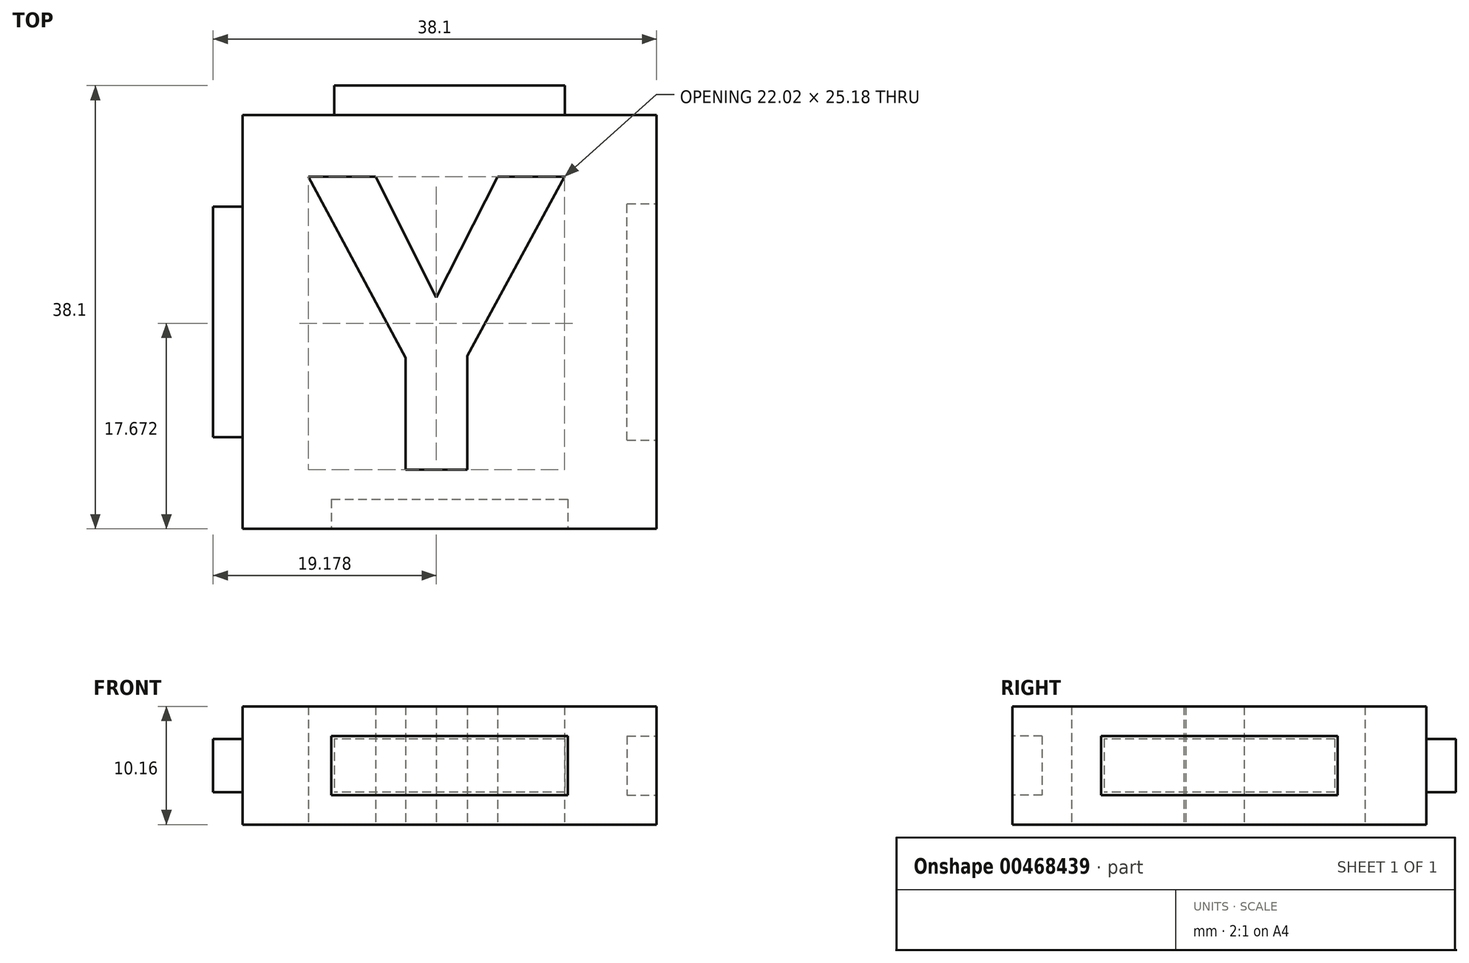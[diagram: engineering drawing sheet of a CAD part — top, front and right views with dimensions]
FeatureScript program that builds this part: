
annotation { "Feature Type Name" : "Feature", "Feature Type Description" : "" }
export const myFeature = defineFeature(function(context is Context, id is Id, definition is map)
    precondition{}
    {
        {
            var Q0;
            Q0=qCreatedBy(makeId("Top.planeOp"),FACE);
            var sketch = newSketch(context, id + "F0", { "sketchPlane" : qUnion([Q0])});
            skLineSegment(sketch, "E0.bottom", {"start": v(-17.78, 17.78) * mm, "end": v(17.78, 17.78) * mm});
            skLineSegment(sketch, "E0.top", {"start": v(-17.78, -17.78) * mm, "end": v(17.78, -17.78) * mm});
            skLineSegment(sketch, "E0.left", {"start": v(-17.78, 17.78) * mm, "end": v(-17.78, -17.78) * mm});
            skLineSegment(sketch, "E0.right", {"start": v(17.78, 17.78) * mm, "end": v(17.78, -17.78) * mm});
            skText(sketch, "E1", { "text": "Y", "fontName": "OpenSans-Bold.ttf"});
            const initialGuessF0  = {"E1": [-0.01215, -0.0127, 1, 0, 0.0254]};
            skSetInitialGuess(sketch, initialGuessF0);
            skSolve(sketch);
        }
        {
            var Q0;
            Q0=qSketchRegion(id+"F0",true);
            extrude(context, id + "F1", {"entities" : qUnion([Q0]), "endBound" : BoundingType.SYMMETRIC, "depth" : 10.16 * mm});
        }
        {
            var Q0;
            Q0=makeQuery(id+"F1.opExtrude","SWEPT_FACE",FACE,{"disambiguationData":[OSD([sQuery(id+"F0.wireOp",EDGE,"E0.bottom")])]});
            var sketch = newSketch(context, id + "F2", { "sketchPlane" : qUnion([Q0])});
            skLineSegment(sketch, "E2.bottom", {"start": v(-9.9, 2.29) * mm, "end": v(9.9, 2.29) * mm});
            skLineSegment(sketch, "E2.top", {"start": v(-9.9, -2.29) * mm, "end": v(9.9, -2.29) * mm});
            skLineSegment(sketch, "E2.left", {"start": v(-9.9, 2.29) * mm, "end": v(-9.9, -2.29) * mm});
            skLineSegment(sketch, "E2.right", {"start": v(9.9, 2.29) * mm, "end": v(9.9, -2.29) * mm});
            skSolve(sketch);
        }
        {
            var Q0;
            Q0=qSketchRegion(id+"F2",true);
            extrude(context, id + "F3", {"entities" : qUnion([Q0]), "operationType" : NewBodyOperationType.ADD, "depth" : 2.54 * mm});
        }
        {
            var Q0;
            Q0=makeQuery(id+"F1.opExtrude","SWEPT_FACE",FACE,{"disambiguationData":[OSD([sQuery(id+"F0.wireOp",EDGE,"E0.left")])]});
            var sketch = newSketch(context, id + "F4", { "sketchPlane" : qUnion([Q0])});
            skLineSegment(sketch, "E3.bottom", {"start": v(-9.9, 2.29) * mm, "end": v(9.9, 2.29) * mm});
            skLineSegment(sketch, "E3.top", {"start": v(-9.9, -2.29) * mm, "end": v(9.9, -2.29) * mm});
            skLineSegment(sketch, "E3.left", {"start": v(-9.9, 2.29) * mm, "end": v(-9.9, -2.29) * mm});
            skLineSegment(sketch, "E3.right", {"start": v(9.9, 2.29) * mm, "end": v(9.9, -2.29) * mm});
            skSolve(sketch);
        }
        {
            var Q0;
            Q0=qSketchRegion(id+"F4",true);
            extrude(context, id + "F5", {"entities" : qUnion([Q0]), "operationType" : NewBodyOperationType.ADD, "depth" : 2.54 * mm});
        }
        {
            var Q0;
            Q0=makeQuery(id+"F1.opExtrude","SWEPT_FACE",FACE,{"disambiguationData":[OSD([sQuery(id+"F0.wireOp",EDGE,"E0.top")])]});
            var sketch = newSketch(context, id + "F6", { "sketchPlane" : qUnion([Q0])});
            skLineSegment(sketch, "E4.bottom", {"start": v(-10.16, 2.54) * mm, "end": v(10.16, 2.54) * mm});
            skLineSegment(sketch, "E4.top", {"start": v(-10.16, -2.54) * mm, "end": v(10.16, -2.54) * mm});
            skLineSegment(sketch, "E4.left", {"start": v(-10.16, 2.54) * mm, "end": v(-10.16, -2.54) * mm});
            skLineSegment(sketch, "E4.right", {"start": v(10.16, 2.54) * mm, "end": v(10.16, -2.54) * mm});
            skSolve(sketch);
        }
        {
            var Q0;
            Q0=qSketchRegion(id+"F6",true);
            extrude(context, id + "F7", {"entities" : qUnion([Q0]), "operationType" : NewBodyOperationType.REMOVE, "oppositeDirection" : true, "depth" : 2.54 * mm});
        }
        {
            var Q0;
            Q0=makeQuery(id+"F1.opExtrude","SWEPT_FACE",FACE,{"disambiguationData":[OSD([sQuery(id+"F0.wireOp",EDGE,"E0.right")])]});
            var sketch = newSketch(context, id + "F8", { "sketchPlane" : qUnion([Q0])});
            skLineSegment(sketch, "E5.bottom", {"start": v(-10.16, 2.54) * mm, "end": v(10.16, 2.54) * mm});
            skLineSegment(sketch, "E5.top", {"start": v(-10.16, -2.54) * mm, "end": v(10.16, -2.54) * mm});
            skLineSegment(sketch, "E5.left", {"start": v(-10.16, 2.54) * mm, "end": v(-10.16, -2.54) * mm});
            skLineSegment(sketch, "E5.right", {"start": v(10.16, 2.54) * mm, "end": v(10.16, -2.54) * mm});
            skSolve(sketch);
        }
        {
            var Q0;
            Q0=qSketchRegion(id+"F8",true);
            extrude(context, id + "F9", {"entities" : qUnion([Q0]), "operationType" : NewBodyOperationType.REMOVE, "oppositeDirection" : true, "depth" : 2.54 * mm});
        }
    });
